# Revit family: Accessory-Towel_Ring-KOHLER-Refined-K-26511_1
name_source: partatom
category: Specialty Equipment
units: mm (PartAtom-declared; Revit-internal decimal feet)

## family parameters
Cut with Voids When Loaded = No
Host = Face
OmniClass Number = 23.31.25.25
OmniClass Title = Towel Bars
Part Type = Normal
Room Calculation Point = No
Round Connector Dimension = Use Diameter
Shared = No

## types (3) — shared parameters
ADA Compliant = No
Assembly Code = C1030200
Date Modified = 11/10/2022
Default Elevation = 42"
Description = Towel ring
Height = 7 5/16"
Length = 6 5/16"
Manufacturer = Kohler Co.
Master Format 2014 = 10 28 00
Master Format 2014 Name = Toilet, Bath, and Laundry Accessories
Material = Premium Metal Construction
Product Documentation Link = https://www.us.kohler.com
Product Name = Refined
Product Page URL = http://www.us.kohler.com
URL = https://www.us.kohler.com
WaterSense Certified = No
Width = 3"

## per-type parameters (varying)
| type | Finish | Model | Type |
| 2BZ-Oil Rubbed Bronze | Kohler-Metal-2BZ-Oil_Rubbed_Bronze | K-26511-2BZ | 1 |
| BN-Vibrant Brushed Nickel | Kohler-Metal-BN-Vibrant_Brushed_Nickel | K-26511-BN | 2 |
| CP-Polished Chrome | Kohler-Metal-CP-Polished_Chrome | K-26511-CP | 3 |

## geometry (parser evidence)
native form markers: Sweep x4
no freeform markers — native parametric forms only
